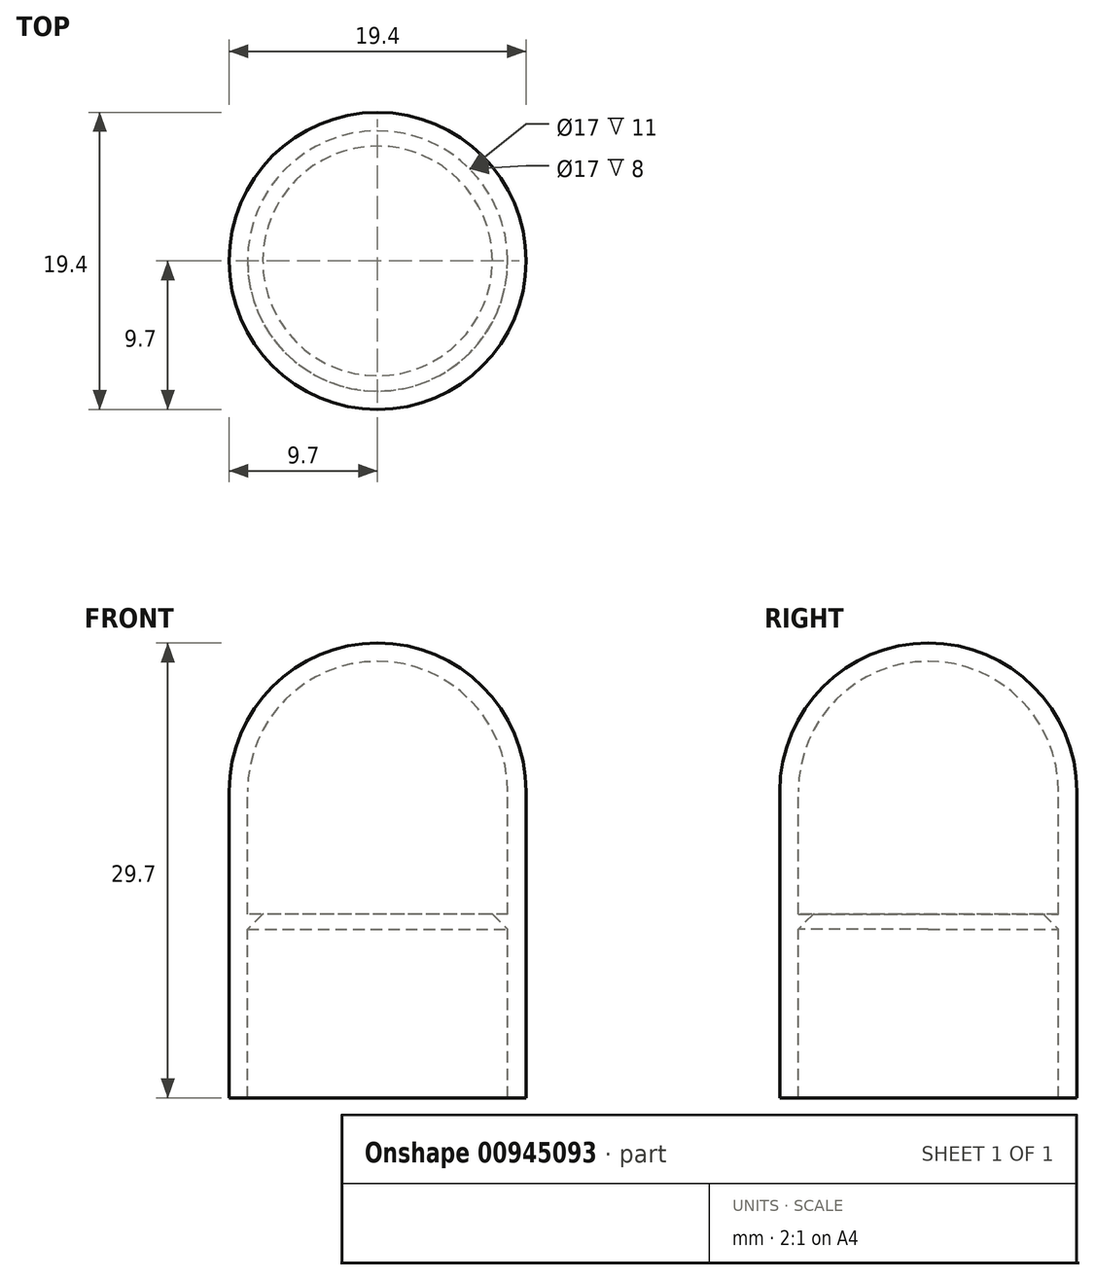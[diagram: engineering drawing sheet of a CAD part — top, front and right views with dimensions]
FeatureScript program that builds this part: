
annotation { "Feature Type Name" : "Feature", "Feature Type Description" : "" }
export const myFeature = defineFeature(function(context is Context, id is Id, definition is map)
    precondition{}
    {
        {
            var Q0;
            Q0=qCreatedBy(makeId("Top.planeOp"),FACE);
            var sketch = newSketch(context, id + "F0", { "sketchPlane" : qUnion([Q0])});
            skCircle(sketch, "E0", {"center": v(0, 0) * mm, "radius": 8.5 * mm});
            skCircle(sketch, "E1", {"center": v(0, 0) * mm, "radius": 9.7 * mm});
            skLineSegment(sketch, "E2", {"start": v(0, 0) * mm, "end": v(-18.37, 0) * mm, "construction": true});
            skLineSegment(sketch, "E3", {"start": v(8.5, 0) * mm, "end": v(9.7, 0) * mm});
            skLineSegment(sketch, "E4", {"start": v(-9.7, 0) * mm, "end": v(-8.5, 0) * mm});
            skCircle(sketch, "E5", {"center": v(0, 0) * mm, "radius": 7.5 * mm});
            skSolve(sketch);
        }
        {
            var Q0;
            {var subQ0=sQuery(id+"F0.wireOp",EDGE,"E3");Q0=makeQuery(id+"F0.imprint","IMPRINT",FACE,{"disambiguationData":[TD([[makeQuery(id+"F0.imprint","IMPRINT",EDGE,{"derivedFrom":subQ0}),-1.0]])]});}
            var Q1;
            {var subQ0=sQuery(id+"F0.wireOp",EDGE,"E3");Q1=makeQuery(id+"F0.imprint","IMPRINT",FACE,{"disambiguationData":[TD([[makeQuery(id+"F0.imprint","IMPRINT",EDGE,{"derivedFrom":subQ0}),1.0]])]});}
            extrude(context, id + "F1", {"entities" : qUnion([Q0, Q1]), "oppositeDirection" : true, "depth" : 20 * mm, "offsetDistance" : 25 * mm});
        }
        {
            var Q0;
            Q0=makeQuery(id+"F0.imprint","IMPRINT",FACE,{"disambiguationData":[TD([[makeQuery(id+"F0.imprint","IMPRINT",EDGE,{"derivedFrom":sQuery(id+"F0.wireOp",EDGE,"E5")}),-1.0]])]});
            extrude(context, id + "F2", {"entities" : qUnion([Q0]), "operationType" : NewBodyOperationType.ADD, "oppositeDirection" : true, "depth" : 10 * mm, "offsetDistance" : 25 * mm, "hasSecondDirection" : true, "secondDirectionOppositeDirection" : true, "secondDirectionDepth" : 8 * mm});
        }
        {
            var Q0;
            Q0=makeQuery(id+"F2.opExtrude","CAP_EDGE",EDGE,{"disambiguationData":[OSD([sQuery(id+"F0.wireOp",EDGE,"E5")])],"isStart":false});
            chamfer(context, id + "F3", {"entities" : qUnion([Q0]), "width" : 2 * mm, "tangentPropagation" : true});
        }
        {
            var Q0;
            {var subQ0=sQuery(id+"F0.wireOp",EDGE,"E3");Q0=makeQuery(id+"F0.imprint","IMPRINT",FACE,{"disambiguationData":[TD([[makeQuery(id+"F0.imprint","IMPRINT",EDGE,{"derivedFrom":subQ0}),1.0]])]});}
            var Q1;
            Q1=sQuery(id+"F0.wireOp",EDGE,"E2");
            revolve(context, id + "F4", {"operationType" : NewBodyOperationType.ADD, "surfaceOperationType" : NewSurfaceOperationType.NEW, "entities" : qUnion([Q0]), "axis" : qUnion([Q1]), "revolveType" : RevolveType.ONE_DIRECTION, "oppositeDirection" : true, "angle" : 180 * degree});
        }
    });
